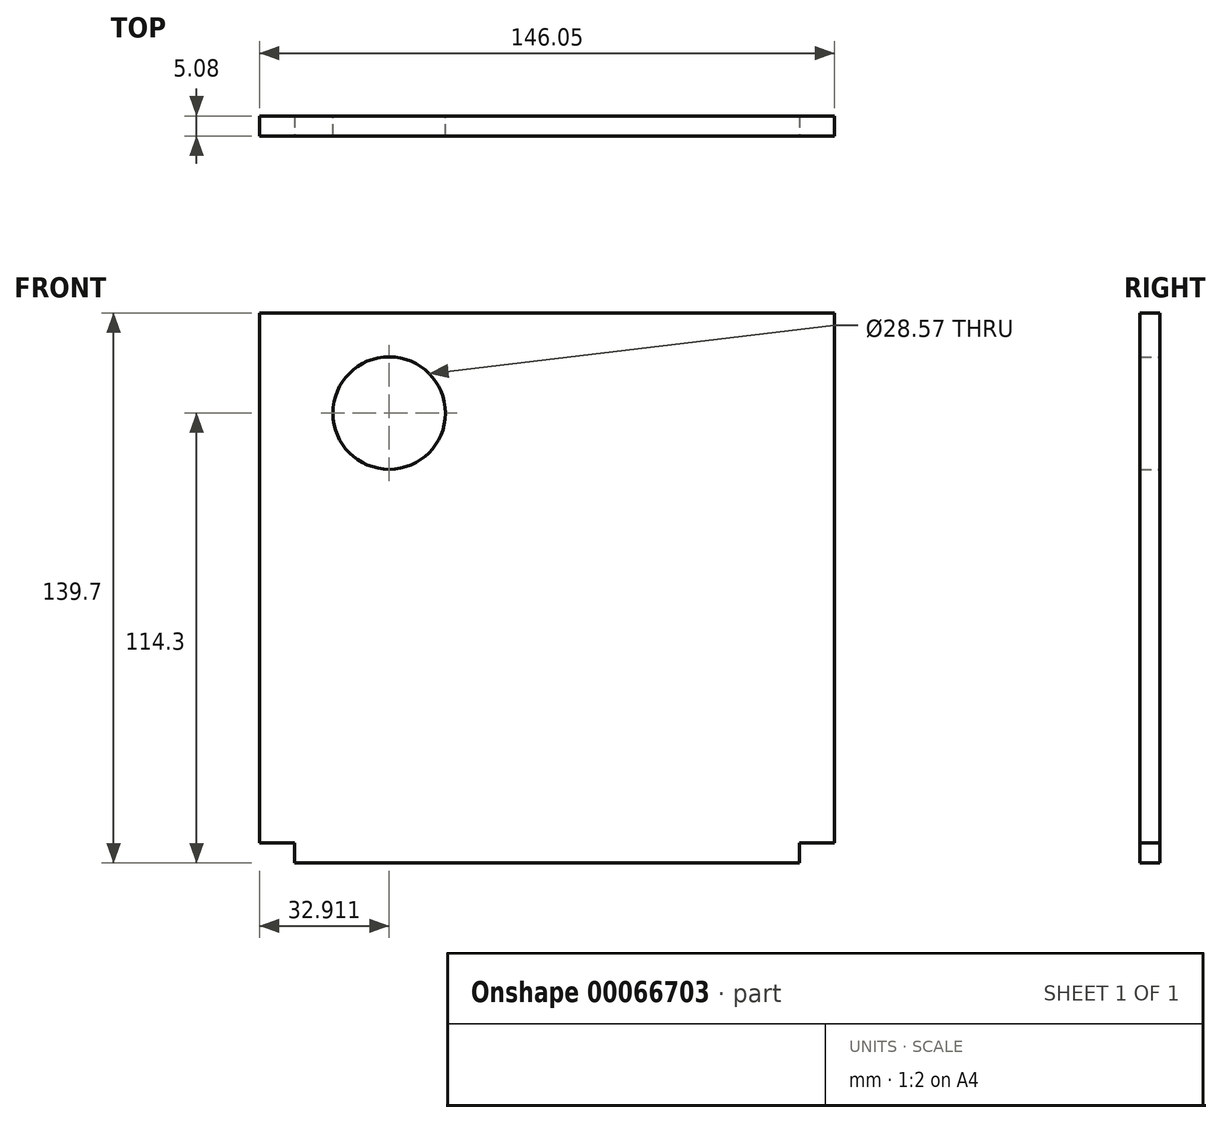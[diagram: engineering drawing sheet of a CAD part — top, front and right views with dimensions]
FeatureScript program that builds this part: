
annotation { "Feature Type Name" : "Feature", "Feature Type Description" : "" }
export const myFeature = defineFeature(function(context is Context, id is Id, definition is map)
    precondition{}
    {
        {
            var Q0;
            Q0=qCreatedBy(makeId("Front.planeOp"),FACE);
            var sketch = newSketch(context, id + "F0", { "sketchPlane" : qUnion([Q0])});
            skLineSegment(sketch, "E0", {"start": v(0, 0) * mm, "end": v(146.05, 0) * mm});
            skLineSegment(sketch, "E1", {"start": v(146.05, 0) * mm, "end": v(146.05, -139.7) * mm});
            skLineSegment(sketch, "E2", {"start": v(146.05, -139.7) * mm, "end": v(0, -139.7) * mm});
            skLineSegment(sketch, "E3", {"start": v(0, -139.7) * mm, "end": v(0, 0) * mm});
            skLineSegment(sketch, "E4", {"start": v(32.91, 0) * mm, "end": v(32.91, -25.4) * mm});
            skLineSegment(sketch, "E5", {"start": v(0, -25.4) * mm, "end": v(32.91, -25.4) * mm});
            skCircle(sketch, "E6", {"center": v(32.91, -25.4) * mm, "radius": 14.29 * mm});
            skSolve(sketch);
        }
        {
            var Q0;
            {var subQ4=sQuery(id+"F0.wireOp",EDGE,"E1");Q0=makeQuery(id+"F0.imprint","IMPRINT",FACE,{"disambiguationData":[TD([[makeQuery(id+"F0.imprint","IMPRINT",EDGE,{"derivedFrom":subQ4}),-1.0]])]});}
            var Q1;
            {var subQ1=sQuery(id+"F0.wireOp",EDGE,"E3");var subQ6=sQuery(id+"F0.wireOp",EDGE,"E0");var subQ9=makeQuery(id+"F0.imprint","INTERSECT",VERTEX,{"derivedFrom":[subQ6,subQ1]});Q1=makeQuery(id+"F0.imprint","IMPRINT",FACE,{"disambiguationData":[TD([[makeQuery(id+"F0.imprint","IMPRINT",EDGE,{"disambiguationData":[TD([[subQ9,-1.0]])],"derivedFrom":subQ6}),-1.0]])]});}
            extrude(context, id + "F1", {"entities" : qUnion([Q0, Q1]), "depth" : 5.08 * mm});
        }
        {
            var Q0;
            Q0=makeQuery(id+"F1.opExtrude","SWEPT_FACE",FACE,{"disambiguationData":[OSD([sQuery(id+"F0.wireOp",EDGE,"E2")])]});
            var sketch = newSketch(context, id + "F2", { "sketchPlane" : qUnion([Q0])});
            skLineSegment(sketch, "E7.bottom", {"start": v(0, 0) * mm, "end": v(8.9, 0) * mm});
            skLineSegment(sketch, "E7.top", {"start": v(0, 5.08) * mm, "end": v(8.9, 5.08) * mm});
            skLineSegment(sketch, "E7.left", {"start": v(0, 0) * mm, "end": v(0, 5.08) * mm});
            skLineSegment(sketch, "E7.right", {"start": v(8.9, 0) * mm, "end": v(8.9, 5.08) * mm});
            skLineSegment(sketch, "E8.bottom", {"start": v(146.05, 0) * mm, "end": v(137.16, 0) * mm});
            skLineSegment(sketch, "E8.top", {"start": v(146.05, 5.08) * mm, "end": v(137.16, 5.08) * mm});
            skLineSegment(sketch, "E8.left", {"start": v(146.05, 0) * mm, "end": v(146.05, 5.08) * mm});
            skLineSegment(sketch, "E8.right", {"start": v(137.16, 0) * mm, "end": v(137.16, 5.08) * mm});
            skSolve(sketch);
        }
        {
            var Q0;
            Q0 = qSketchRegion(id + "F2", true);
            extrude(context, id + "F3", {"entities" : qUnion([Q0]), "operationType" : NewBodyOperationType.REMOVE, "oppositeDirection" : true, "depth" : 5.08 * mm});
        }
    });
